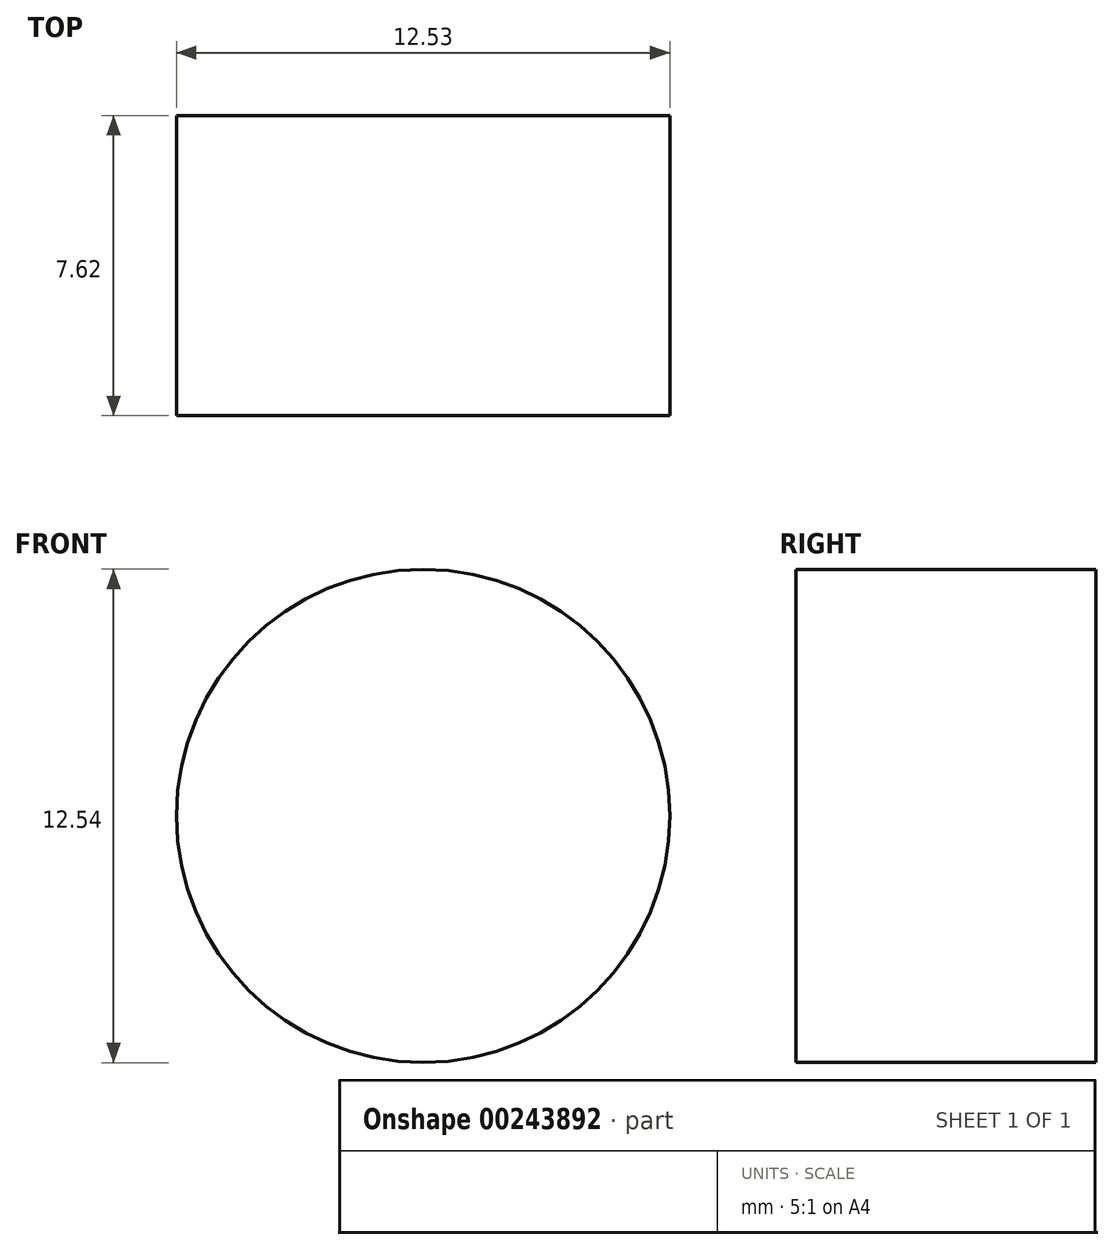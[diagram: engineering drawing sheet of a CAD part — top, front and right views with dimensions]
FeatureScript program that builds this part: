
annotation { "Feature Type Name" : "Feature", "Feature Type Description" : "" }
export const myFeature = defineFeature(function(context is Context, id is Id, definition is map)
    precondition{}
    {
        {
            var Q0;
            Q0=qCreatedBy(makeId("Front.planeOp"),FACE);
            var sketch = newSketch(context, id + "F0", { "sketchPlane" : qUnion([Q0])});
            skLineSegment(sketch, "E0.bottom", {"start": v(-126.1, 51.64) * mm, "end": v(126.51, 51.64) * mm});
            skLineSegment(sketch, "E0.top", {"start": v(-126.1, -49.96) * mm, "end": v(126.51, -49.96) * mm});
            skLineSegment(sketch, "E0.left", {"start": v(-126.1, 51.64) * mm, "end": v(-126.1, -49.96) * mm});
            skLineSegment(sketch, "E0.right", {"start": v(126.51, 51.64) * mm, "end": v(126.51, -49.96) * mm});
            skSolve(sketch);
        }
        {
            var Q0;
            Q0=makeQuery(id+"F0.imprint","IMPRINT",FACE,{"disambiguationData":[TD([[makeQuery(id+"F0.imprint","IMPRINT",EDGE,{"derivedFrom":sQuery(id+"F0.wireOp",EDGE,"E0.bottom")}),-1.0]])]});
            extrude(context, id + "F1", {"entities" : qUnion([Q0]), "depth" : 7.62 * mm});
        }
        {
            var Q0;
            Q0=makeQuery(id+"F1.opExtrude","CAP_FACE",FACE,{"disambiguationData":[OSD([sQuery(id+"F0.wireOp",EDGE,"E0.bottom"),sQuery(id+"F0.wireOp",EDGE,"E0.top"),sQuery(id+"F0.wireOp",EDGE,"E0.left"),sQuery(id+"F0.wireOp",EDGE,"E0.right")])],"isStart":false});
            var sketch = newSketch(context, id + "F2", { "sketchPlane" : qUnion([Q0])});
            skCircle(sketch, "E1", {"center": v(-55.96, 0) * mm, "radius": 6.27 * mm});
            skCircle(sketch, "E2.MirrorC", {"center": v(55.96, 0) * mm, "radius": 6.27 * mm});
            skSolve(sketch);
        }
        {
            var Q0;
            Q0=makeQuery(id+"F2.imprint","IMPRINT",FACE,{"disambiguationData":[TD([[makeQuery(id+"F2.imprint","IMPRINT",EDGE,{"derivedFrom":sQuery(id+"F2.wireOp",EDGE,"E1")}),1.0]])]});
            var Q1;
            Q1=makeQuery(id+"F2.imprint","IMPRINT",FACE,{"disambiguationData":[TD([[makeQuery(id+"F2.imprint","IMPRINT",EDGE,{"derivedFrom":sQuery(id+"F2.wireOp",EDGE,"E2.MirrorC")}),-1.0]])]});
            extrude(context, id + "F3", {"entities" : qUnion([Q0, Q1]), "operationType" : NewBodyOperationType.REMOVE, "oppositeDirection" : true, "depth" : 76.2 * mm});
        }
    });
